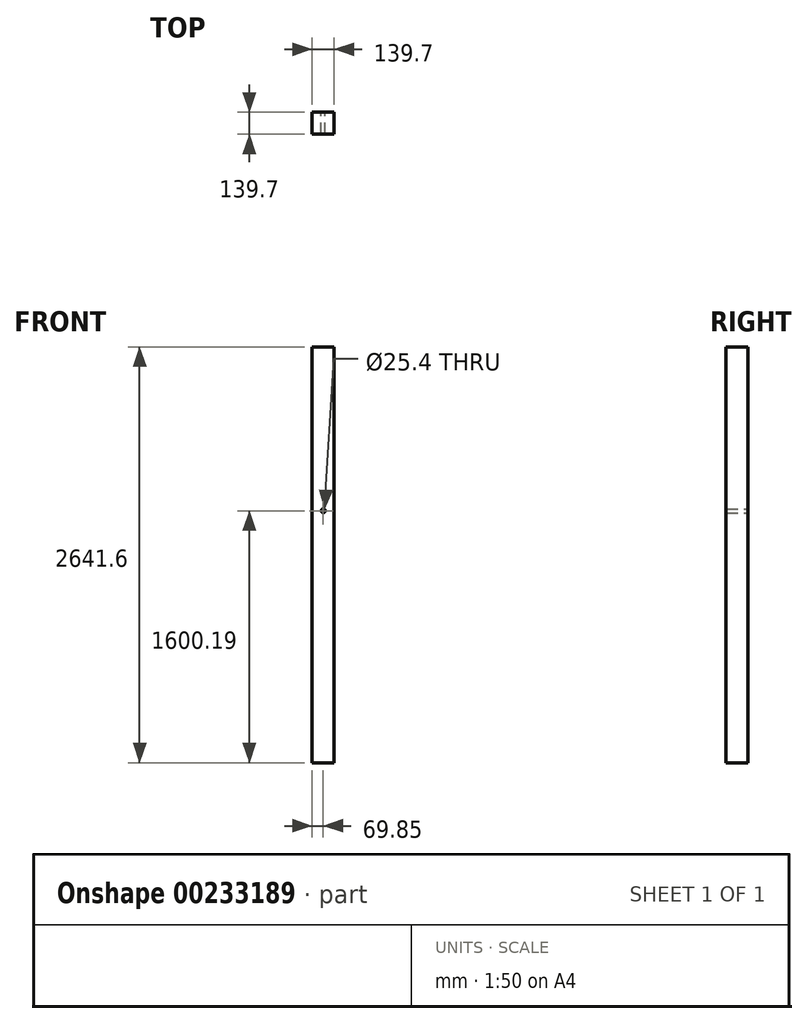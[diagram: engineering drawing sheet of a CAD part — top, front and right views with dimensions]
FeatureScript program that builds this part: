
annotation { "Feature Type Name" : "Feature", "Feature Type Description" : "" }
export const myFeature = defineFeature(function(context is Context, id is Id, definition is map)
    precondition{}
    {
        {
            var Q0;
            Q0=qCreatedBy(makeId("Front.planeOp"),FACE);
            var sketch = newSketch(context, id + "F0", { "sketchPlane" : qUnion([Q0])});
            skLineSegment(sketch, "E0.bottom", {"start": v(-139.7, 2426) * mm, "end": v(0, 2426) * mm});
            skLineSegment(sketch, "E0.top", {"start": v(-139.7, -215.6) * mm, "end": v(0, -215.6) * mm});
            skLineSegment(sketch, "E0.left", {"start": v(-139.7, 2426) * mm, "end": v(-139.7, -215.6) * mm});
            skLineSegment(sketch, "E0.right", {"start": v(0, 2426) * mm, "end": v(0, -215.6) * mm});
            skCircle(sketch, "E1", {"center": v(-69.85, 1384.6) * mm, "radius": 12.7 * mm});
            skSolve(sketch);
        }
        {
            var Q0;
            Q0 = qSketchRegion(id + "F0", true);
            extrude(context, id + "F1", {"entities" : qUnion([Q0]), "depth" : 139.7 * mm});
        }
    });
